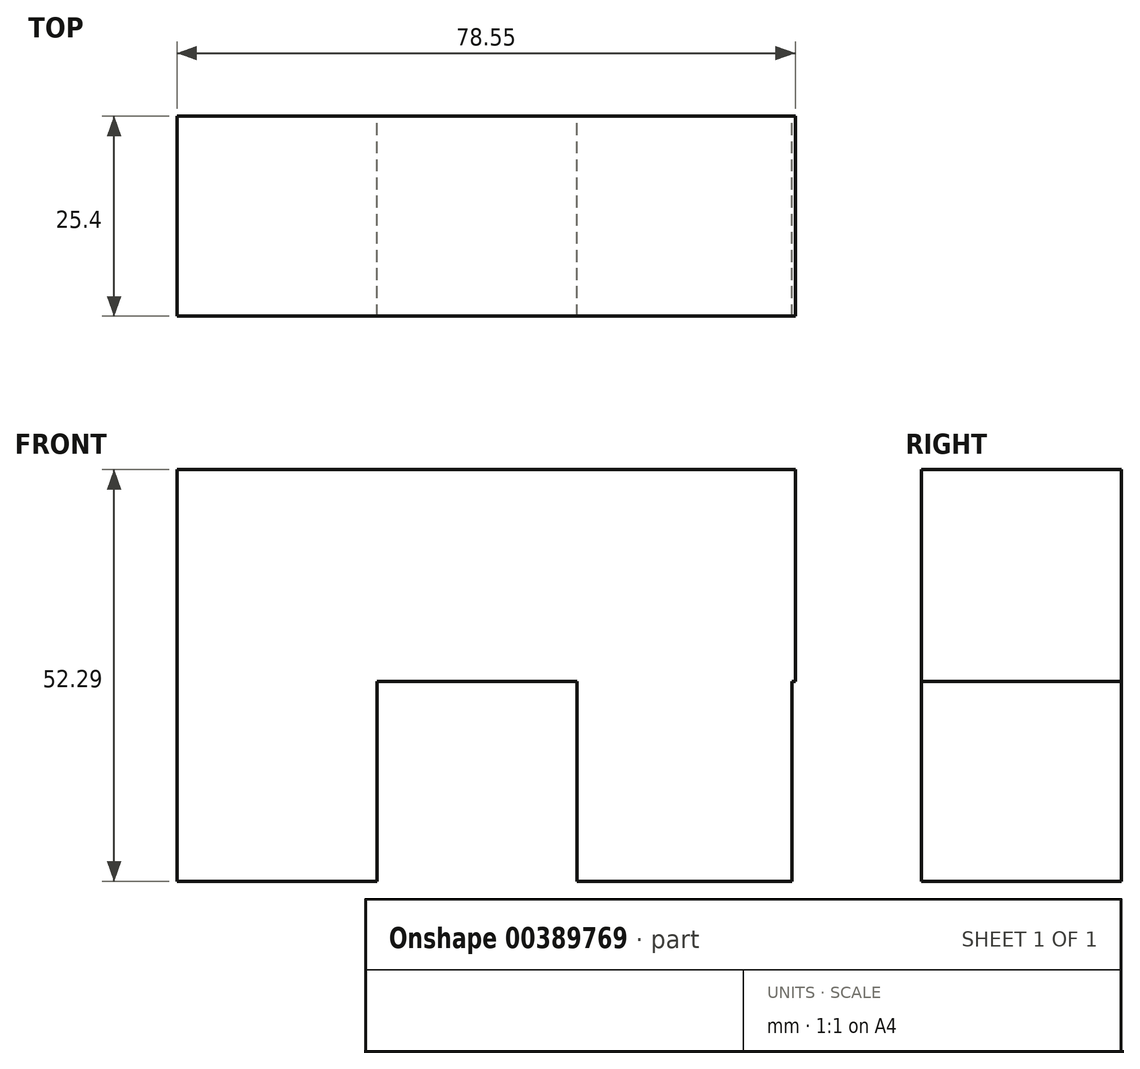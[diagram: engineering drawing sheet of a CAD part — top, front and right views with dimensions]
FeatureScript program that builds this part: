
annotation { "Feature Type Name" : "Feature", "Feature Type Description" : "" }
export const myFeature = defineFeature(function(context is Context, id is Id, definition is map)
    precondition{}
    {
        {
            var Q0;
            Q0=qCreatedBy(makeId("Front.planeOp"),FACE);
            var sketch = newSketch(context, id + "F0", { "sketchPlane" : qUnion([Q0])});
            skLineSegment(sketch, "E0.bottom", {"start": v(-50.8, 0) * mm, "end": v(-25.4, 0) * mm});
            skLineSegment(sketch, "E0.top", {"start": v(-50.8, 25.4) * mm, "end": v(-25.4, 25.4) * mm});
            skLineSegment(sketch, "E0.left", {"start": v(-50.8, 0) * mm, "end": v(-50.8, 25.4) * mm});
            skLineSegment(sketch, "E0.right", {"start": v(-25.4, 0) * mm, "end": v(-25.4, 25.4) * mm});
            skLineSegment(sketch, "E1.top", {"start": v(-50.8, 52.3) * mm, "end": v(-25.4, 52.3) * mm});
            skLineSegment(sketch, "E1.left", {"start": v(-50.8, 25.4) * mm, "end": v(-50.8, 52.3) * mm});
            skLineSegment(sketch, "E1.right", {"start": v(-25.4, 25.4) * mm, "end": v(-25.4, 52.3) * mm});
            skLineSegment(sketch, "E2.bottom", {"start": v(-25.4, 52.3) * mm, "end": v(0, 52.3) * mm});
            skLineSegment(sketch, "E2.top", {"start": v(-25.4, 25.4) * mm, "end": v(0, 25.4) * mm});
            skLineSegment(sketch, "E2.left", {"start": v(-25.4, 52.3) * mm, "end": v(-25.4, 25.4) * mm});
            skLineSegment(sketch, "E2.right", {"start": v(0, 52.3) * mm, "end": v(0, 25.4) * mm});
            skLineSegment(sketch, "E3.bottom", {"start": v(0, 25.4) * mm, "end": v(27.32, 25.4) * mm});
            skLineSegment(sketch, "E3.top", {"start": v(0, 0) * mm, "end": v(27.32, 0) * mm});
            skLineSegment(sketch, "E3.left", {"start": v(0, 25.4) * mm, "end": v(0, 0) * mm});
            skLineSegment(sketch, "E3.right", {"start": v(27.32, 25.4) * mm, "end": v(27.32, 0) * mm});
            skLineSegment(sketch, "E4.bottom", {"start": v(0, 25.4) * mm, "end": v(27.75, 25.4) * mm});
            skLineSegment(sketch, "E4.top", {"start": v(0, 52.3) * mm, "end": v(27.75, 52.3) * mm});
            skLineSegment(sketch, "E4.left", {"start": v(0, 25.4) * mm, "end": v(0, 52.3) * mm});
            skLineSegment(sketch, "E4.right", {"start": v(27.75, 25.4) * mm, "end": v(27.75, 52.3) * mm});
            skSolve(sketch);
        }
        {
            var Q0;
            Q0=makeQuery(id+"F0.imprint","IMPRINT",FACE,{"disambiguationData":[TD([[makeQuery(id+"F0.imprint","IMPRINT",EDGE,{"derivedFrom":sQuery(id+"F0.wireOp",EDGE,"E0.top")}),1.0]])]});
            var Q1;
            Q1=makeQuery(id+"F0.imprint","IMPRINT",FACE,{"disambiguationData":[TD([[makeQuery(id+"F0.imprint","IMPRINT",EDGE,{"derivedFrom":sQuery(id+"F0.wireOp",EDGE,"E0.bottom")}),1.0]])]});
            var Q2;
            Q2=makeQuery(id+"F0.imprint","IMPRINT",FACE,{"disambiguationData":[TD([[makeQuery(id+"F0.imprint","IMPRINT",EDGE,{"derivedFrom":sQuery(id+"F0.wireOp",EDGE,"E2.bottom")}),-1.0]])]});
            var Q3;
            Q3=makeQuery(id+"F0.imprint","IMPRINT",FACE,{"disambiguationData":[TD([[makeQuery(id+"F0.imprint","IMPRINT",EDGE,{"derivedFrom":sQuery(id+"F0.wireOp",EDGE,"E4.top")}),-1.0]])]});
            var Q4;
            Q4=makeQuery(id+"F0.imprint","IMPRINT",FACE,{"disambiguationData":[TD([[makeQuery(id+"F0.imprint","IMPRINT",EDGE,{"derivedFrom":sQuery(id+"F0.wireOp",EDGE,"E3.top")}),1.0]])]});
            extrude(context, id + "F1", {"entities" : qUnion([Q0, Q1, Q2, Q3, Q4]), "depth" : 25.4 * mm});
        }
    });
